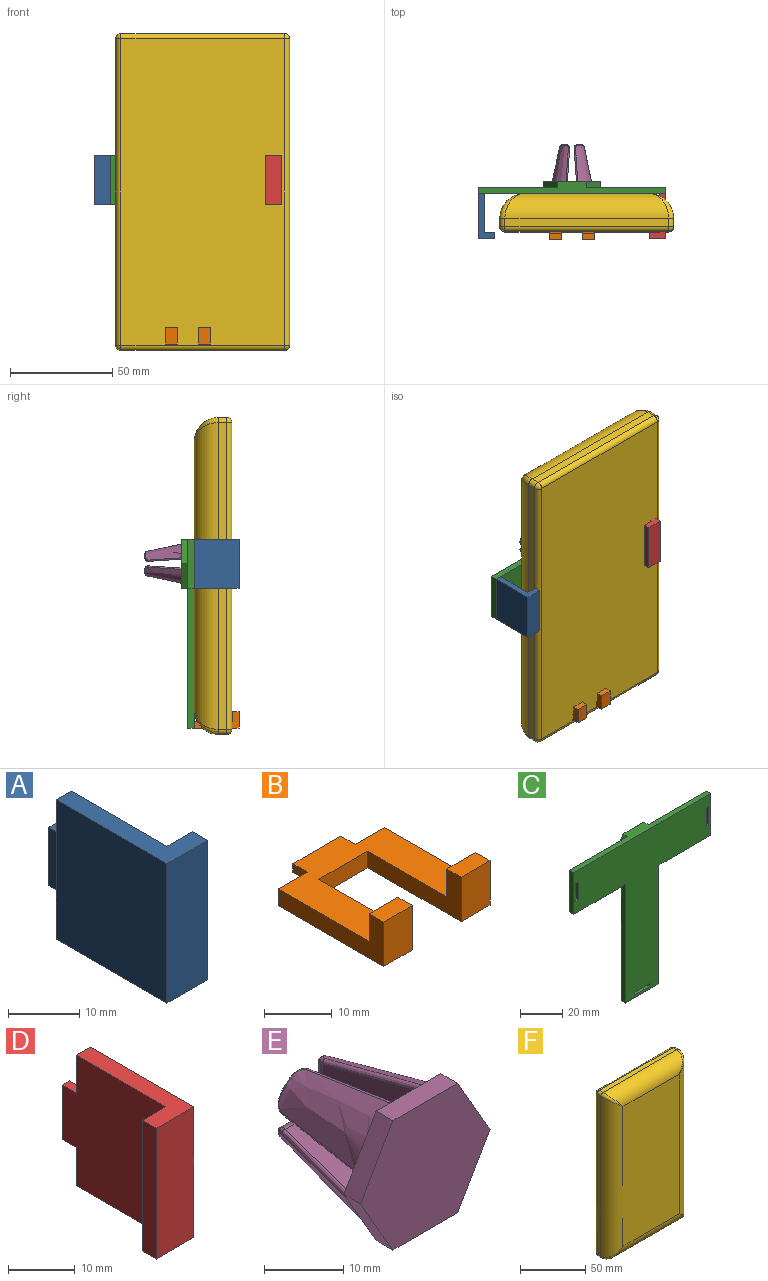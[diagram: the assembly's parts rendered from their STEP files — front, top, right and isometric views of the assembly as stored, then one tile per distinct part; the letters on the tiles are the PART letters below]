
ASSEMBLY  parts=6 mates=5
PART A: 12 faces, bbox 8x25x24 mm
  f0: plane 22x8mm, normal (0,0,-1), area 81mm2, adj f1,f4,f5,f6,f7,f11
  f1: plane 24x22mm, normal (1,0,0), area 486mm2, adj f0,f2,f3,f7,f8,f10,f11
  f2: plane 22x8mm, normal (0,0,1), area 81mm2, adj f1,f4,f5,f6,f7,f11
  f3: plane 10x1.5mm, normal (0,1,0), area 15mm2, adj f1,f8,f9,f10
  f4: plane 24x22mm, normal (-1,0,0), area 528mm2, adj f0,f2,f6,f11
  f5: plane 24x3mm, normal (1,0,0), area 72mm2, adj f0,f2,f6,f7
  f6: plane 24x8mm, normal (0,-1,0), area 192mm2, adj f0,f2,f4,f5
  f7: plane 24x5mm, normal (0,1,0), area 120mm2, adj f0,f1,f2,f5
  f8: plane 3x1.5mm, normal (0,0,1), area 4.5mm2, adj f1,f3,f9,f11
  f9: plane 10x3mm, normal (-1,0,0), area 30mm2, adj f3,f8,f10,f11
  f10: plane 3x1.5mm, normal (0,0,-1), area 4.5mm2, adj f1,f3,f9,f11
  f11: plane 24x3mm, normal (0,1,0), area 57mm2, adj f0,f1,f2,f4,f8,f9,f10
PART B: 18 faces, bbox 22.2x25x8 mm
  f0: plane 10x1.5mm, normal (0,1,0), area 15mm2, adj f1,f2,f3,f4
  f1: plane 22.2x22mm, normal (0,0,1), area 283.5mm2, adj f0,f3,f4,f5,f6,f7,f9,f12
  f2: plane 10x3mm, normal (0,0,-1), area 30mm2, adj f0,f3,f4,f5
  f3: plane 3x1.5mm, normal (-1,0,0), area 4.5mm2, adj f0,f1,f2,f5
  f4: plane 3x1.5mm, normal (1,0,0), area 4.5mm2, adj f0,f1,f2,f5
  f5: plane 22.2x3mm, normal (0,1,0), area 51.6mm2, adj f1,f2,f3,f4,f7,f8,f16
  f6: plane 19.5x8mm, normal (1,0,0), area 73.5mm2, adj f1,f8,f9,f10,f11,f17
  f7: plane 22x8mm, normal (-1,0,0), area 81mm2, adj f1,f5,f8,f9,f10,f11
  f8: plane 22.2x22mm, normal (0,0,-1), area 289.5mm2, adj f5,f6,f7,f11,f12,f15,f16,f17
  f9: plane 6x5mm, normal (0,1,0), area 30mm2, adj f1,f6,f7,f10
  f10: plane 6x3mm, normal (0,0,1), area 18mm2, adj f6,f7,f9,f11
  f11: plane 8x6mm, normal (0,-1,0), area 48mm2, adj f6,f7,f8,f10
  f12: plane 19.5x8mm, normal (-1,0,0), area 73.5mm2, adj f1,f8,f13,f14,f15,f17
  f13: plane 6x5mm, normal (0,1,0), area 30mm2, adj f1,f12,f14,f16
  f14: plane 6x3mm, normal (0,0,1), area 18mm2, adj f12,f13,f15,f16
  f15: plane 8x6mm, normal (0,-1,0), area 48mm2, adj f8,f12,f14,f16
  f16: plane 22x8mm, normal (1,0,0), area 81mm2, adj f1,f5,f8,f13,f14,f15
  f17: plane 10.2x3mm, normal (0,-1,0), area 30.6mm2, adj f1,f6,f8,f12
PART C: 35 faces, bbox 91.5x6x92.5 mm
  f0: plane 68.5x3mm, normal (-1,0,0), area 205.5mm2, adj f2,f3,f4,f5
  f1: plane 68.5x3mm, normal (1,0,0), area 205.5mm2, adj f2,f3,f4,f9
  f2: plane 22.2x3mm, normal (0,0,-1), area 66.6mm2, adj f0,f1,f3,f4
  f3: plane 92.5x91.5mm, normal (0,1,0), area 3169.4mm2, adj f0,f1,f2,f5,f6,f7,f8,f9
  f4: plane 92.5x91.5mm, normal (0,-1,0), area 3668.2mm2, adj f0,f1,f2,f5,f6,f7,f8,f9
  f5: plane 34.65x3mm, normal (0,0,-1), area 103.9mm2, adj f0,f3,f4,f8
  f6: plane 24x3mm, normal (1,0,0), area 72mm2, adj f3,f4,f7,f9
  f7: plane 91.5x6mm, normal (0,0,1), area 316.1mm2, adj f3,f4,f6,f8,f16,f17,f21
  f8: plane 24x3mm, normal (-1,0,0), area 72mm2, adj f3,f4,f5,f7
  f9: plane 34.65x3mm, normal (0,0,-1), area 103.9mm2, adj f1,f3,f4,f6
  f10: plane 10.1x5.83mm, normal (0.87,0,-0.5), area 35mm2, adj f11,f20,f21,f22
  f11: plane 10.1x5.83mm, normal (0.87,0,0.5), area 35mm2, adj f10,f12,f21,f22
  f12: plane 11.66x3mm, normal (0,0,1), area 35mm2, adj f11,f13,f21,f22
  f13: plane 10.1x5.83mm, normal (-0.87,0,0.5), area 35mm2, adj f12,f14,f21,f22
  f14: plane 10.1x5.83mm, normal (-0.87,0,-0.5), area 35mm2, adj f13,f20,f21,f22
  f15: plane 12x6.93mm, normal (-0.87,0,-0.5), area 41.6mm2, adj f3,f16,f19,f21
  f16: plane 12x6.93mm, normal (-0.87,0,0.5), area 41.6mm2, adj f3,f7,f15,f21
  f17: plane 12x6.93mm, normal (0.87,0,0.5), area 41.6mm2, adj f3,f7,f18,f21
  f18: plane 12x6.93mm, normal (0.87,0,-0.5), area 41.6mm2, adj f3,f17,f19,f21
  f19: plane 13.86x3mm, normal (0,0,-1), area 41.6mm2, adj f3,f15,f18,f21
  f20: plane 11.66x3mm, normal (0,0,-1), area 35mm2, adj f10,f14,f21,f22
  f21: plane 27.71x24mm, normal (0,1,0), area 145.5mm2, adj f7,f10,f11,f12,f13,f14,f15,f16
  f22: plane 23.33x20.2mm, normal (0,1,0), area 353.4mm2, adj f10,f11,f12,f13,f14,f20
  f23: plane 10.1x3mm, normal (1,0,0), area 30.3mm2, adj f3,f4,f24,f25
  f24: plane 3x1.6mm, normal (0,0,-1), area 4.8mm2, adj f3,f4,f23,f26
  f25: plane 3x1.6mm, normal (0,0,1), area 4.8mm2, adj f3,f4,f23,f26
  f26: plane 10.1x3mm, normal (-1,0,0), area 30.3mm2, adj f3,f4,f24,f25
  f27: plane 10.1x3mm, normal (0,0,1), area 30.3mm2, adj f3,f4,f28,f29
  f28: plane 3x1.6mm, normal (1,0,0), area 4.8mm2, adj f3,f4,f27,f30
  f29: plane 3x1.6mm, normal (-1,0,0), area 4.8mm2, adj f3,f4,f27,f30
  f30: plane 10.1x3mm, normal (0,0,-1), area 30.3mm2, adj f3,f4,f28,f29
  f31: plane 10.1x3mm, normal (1,0,0), area 30.3mm2, adj f3,f4,f32,f33
  f32: plane 3x1.6mm, normal (0,0,-1), area 4.8mm2, adj f3,f4,f31,f34
  f33: plane 3x1.6mm, normal (0,0,1), area 4.8mm2, adj f3,f4,f31,f34
  f34: plane 10.1x3mm, normal (-1,0,0), area 30.3mm2, adj f3,f4,f32,f33
PART D: 12 faces, bbox 8x25x24 mm
  f0: plane 22x8mm, normal (0,0,-1), area 81mm2, adj f1,f3,f5,f6,f7,f11
  f1: plane 24x22mm, normal (1,0,0), area 528mm2, adj f0,f4,f6,f11
  f2: plane 10x1.5mm, normal (0,1,0), area 15mm2, adj f3,f8,f9,f10
  f3: plane 24x22mm, normal (-1,0,0), area 486mm2, adj f0,f2,f4,f7,f8,f10,f11
  f4: plane 22x8mm, normal (0,0,1), area 81mm2, adj f1,f3,f5,f6,f7,f11
  f5: plane 24x3mm, normal (-1,0,0), area 72mm2, adj f0,f4,f6,f7
  f6: plane 24x8mm, normal (0,-1,0), area 192mm2, adj f0,f1,f4,f5
  f7: plane 24x5mm, normal (0,1,0), area 120mm2, adj f0,f3,f4,f5
  f8: plane 3x1.5mm, normal (0,0,-1), area 4.5mm2, adj f2,f3,f9,f11
  f9: plane 10x3mm, normal (1,0,0), area 30mm2, adj f2,f8,f10,f11
  f10: plane 3x1.5mm, normal (0,0,1), area 4.5mm2, adj f2,f3,f9,f11
  f11: plane 24x3mm, normal (0,1,0), area 57mm2, adj f0,f1,f3,f4,f8,f9,f10
PART E: 60 faces, bbox 23.2x23.4x20.6 mm
  f0: bspline ~17.61x8.12mm, area 143.4mm2, adj f4,f18,f19,f20,f48,f52
  f1: bspline ~17.61x8.12mm, area 143.4mm2, adj f4,f22,f23,f24,f43,f47
  f2: bspline ~17.61x8.12mm, area 143.4mm2, adj f4,f26,f27,f28,f38,f42
  f3: bspline ~17.61x8.12mm, area 143.4mm2, adj f4,f30,f31,f32,f33,f37
  f4: plane 23.15x20.06mm, normal (0,1,0), area 188.5mm2, adj f0,f1,f2,f3,f6,f7,f9,f10
  f5: plane 2.36x2.36mm, normal (0,1,0), area 3.3mm2, adj f31,f34,f36
  f6: plane 16.4x7.48mm, normal (-1,-0.07,0), area 85.4mm2, adj f4,f29,f32,f34
  f7: plane 16.4x7.48mm, normal (0,-0.07,-1), area 85.4mm2, adj f4,f29,f30,f36
  f8: plane 2.36x2.36mm, normal (0,1,0), area 3.3mm2, adj f27,f39,f41
  f9: plane 16.4x7.48mm, normal (1,-0.07,0), area 85.4mm2, adj f4,f25,f28,f39
  f10: plane 16.4x7.48mm, normal (0,-0.07,-1), area 85.4mm2, adj f4,f25,f26,f41
  f11: plane 2.36x2.36mm, normal (0,1,0), area 3.3mm2, adj f23,f44,f46
  f12: plane 16.4x7.48mm, normal (-1,-0.07,0), area 85.4mm2, adj f4,f21,f24,f44
  f13: plane 16.4x7.48mm, normal (0,-0.07,1), area 85.4mm2, adj f4,f21,f22,f46
  f14: plane 2.36x2.36mm, normal (0,1,0), area 3.3mm2, adj f19,f49,f51
  f15: plane 16.4x7.48mm, normal (0,-0.07,1), area 85.4mm2, adj f4,f17,f20,f49
  f16: plane 16.4x7.48mm, normal (1,-0.07,0), area 85.4mm2, adj f4,f17,f18,f51
  f17: cylinder r=0.5mm len=16.41mm, axis (-0.07,-1,-0.07), area 12.9mm2, adj f4,f15,f16,f50
  f18: bspline ~22.72x5.45mm, area 15.7mm2, adj f0,f4,f16,f52
  f19: bspline ~3.89x3.54mm, area 2.4mm2, adj f0,f14,f48,f52
  f20: bspline ~22.72x5.45mm, area 15.7mm2, adj f0,f4,f15,f48
  f21: cylinder r=0.5mm len=16.41mm, axis (0.07,-1,-0.07), area 12.9mm2, adj f4,f12,f13,f45
  f22: bspline ~22.72x5.45mm, area 15.7mm2, adj f1,f4,f13,f47
  f23: bspline ~3.89x3.54mm, area 2.4mm2, adj f1,f11,f43,f47
  f24: bspline ~22.72x5.45mm, area 15.7mm2, adj f1,f4,f12,f43
  f25: cylinder r=0.5mm len=16.41mm, axis (-0.07,-1,0.07), area 12.9mm2, adj f4,f9,f10,f40
  f26: bspline ~22.72x5.45mm, area 15.7mm2, adj f2,f4,f10,f42
  f27: bspline ~3.89x3.54mm, area 2.4mm2, adj f2,f8,f38,f42
  f28: bspline ~22.72x5.45mm, area 15.7mm2, adj f2,f4,f9,f38
  f29: cylinder r=0.5mm len=16.41mm, axis (-0.07,1,-0.07), area 12.9mm2, adj f4,f6,f7,f35
  f30: bspline ~20.18x4.91mm, area 15.7mm2, adj f3,f4,f7,f37
  f31: bspline ~3.62x3.43mm, area 2.4mm2, adj f3,f5,f33,f37
  f32: bspline ~20.18x4.91mm, area 15.7mm2, adj f3,f4,f6,f33
  f33: bspline ~2.03x1.75mm, area 1.9mm2, adj f3,f31,f32,f34
  f34: cylinder r=1.5mm len=4mm, axis (0,0,-1), area 7.8mm2, adj f5,f6,f33,f35
  f35: bspline ~1.76x1.5mm, area 0.9mm2, adj f29,f34,f36
  f36: cylinder r=1.5mm len=4mm, axis (-1,0,0), area 7.8mm2, adj f5,f7,f35,f37
  f37: bspline ~1.99x1.93mm, area 1.9mm2, adj f3,f30,f31,f36
  f38: bspline ~1.99x1.93mm, area 1.9mm2, adj f2,f27,f28,f39
  f39: cylinder r=1.5mm len=4mm, axis (0,0,-1), area 7.8mm2, adj f8,f9,f38,f40
  f40: bspline ~1.76x1.5mm, area 0.9mm2, adj f25,f39,f41
  f41: cylinder r=1.5mm len=4mm, axis (1,0,0), area 7.8mm2, adj f8,f10,f40,f42
  f42: bspline ~2.03x1.75mm, area 1.9mm2, adj f2,f26,f27,f41
  f43: bspline ~1.99x1.93mm, area 1.9mm2, adj f1,f23,f24,f44
  f44: cylinder r=1.5mm len=4mm, axis (0,0,1), area 7.8mm2, adj f11,f12,f43,f45
  f45: bspline ~1.76x1.5mm, area 0.9mm2, adj f21,f44,f46
  f46: cylinder r=1.5mm len=4mm, axis (-1,0,0), area 7.8mm2, adj f11,f13,f45,f47
  f47: bspline ~2.03x1.75mm, area 1.9mm2, adj f1,f22,f23,f46
  f48: bspline ~1.99x1.93mm, area 1.9mm2, adj f0,f19,f20,f49
  f49: cylinder r=1.5mm len=4mm, axis (1,0,0), area 7.8mm2, adj f14,f15,f48,f50
  f50: bspline ~1.76x1.5mm, area 0.9mm2, adj f17,f49,f51
  f51: cylinder r=1.5mm len=4mm, axis (0,0,1), area 7.8mm2, adj f14,f16,f50,f52
  f52: bspline ~2.03x1.75mm, area 1.9mm2, adj f0,f18,f19,f51
  f53: plane 11.55x3mm, normal (0,0,1), area 34.6mm2, adj f4,f54,f58,f59
  f54: plane 10x5.77mm, normal (0.87,0,0.5), area 34.6mm2, adj f4,f53,f55,f59
  f55: plane 10x5.77mm, normal (0.87,0,-0.5), area 34.6mm2, adj f4,f54,f56,f59
  f56: plane 11.55x3mm, normal (0,0,-1), area 34.6mm2, adj f4,f55,f57,f59
  f57: plane 10x5.77mm, normal (-0.87,0,-0.5), area 34.6mm2, adj f4,f56,f58,f59
  f58: plane 10x5.77mm, normal (-0.87,0,0.5), area 34.6mm2, adj f4,f53,f57,f59
  f59: plane 23.09x20mm, normal (0,-1,0), area 346.4mm2, adj f53,f54,f55,f56,f57,f58
PART F: 26 faces, bbox 85x18.5x155 mm
  f0: plane 80x4mm, normal (0,0,1), area 320mm2, adj f6,f9,f11,f20
  f1: plane 150x4mm, normal (-1,0,0), area 600mm2, adj f6,f7,f12,f19
  f2: plane 80x4mm, normal (0,0,-1), area 320mm2, adj f7,f8,f16,f23
  f3: plane 150x4mm, normal (1,0,0), area 600mm2, adj f8,f9,f15,f24
  f4: plane 131x61mm, normal (0,-1,0), area 7991mm2, adj f19,f20,f23,f24
  f5: plane 150x80mm, normal (0,1,0), area 12000mm2, adj f11,f12,f15,f16
  f6: cylinder r=2.5mm len=4mm, axis (0,-1,0), area 15.7mm2, adj f0,f1,f10,f18
  f7: cylinder r=2.5mm len=4mm, axis (0,1,0), area 15.7mm2, adj f1,f2,f14,f21
  f8: cylinder r=2.5mm len=4mm, axis (0,-1,0), area 15.7mm2, adj f2,f3,f17,f25
  f9: cylinder r=2.5mm len=4mm, axis (0,1,0), area 15.7mm2, adj f0,f3,f13,f22
  f10: sphere r=2.5mm, area 9.8mm2, adj f6,f11,f12
  f11: cylinder r=2.5mm len=80mm, axis (-1,0,0), area 314.2mm2, adj f0,f5,f10,f13
  f12: cylinder r=2.5mm len=150mm, axis (0,0,-1), area 589mm2, adj f1,f5,f10,f14
  f13: sphere r=2.5mm, area 9.8mm2, adj f9,f11,f15
  f14: sphere r=2.5mm, area 9.8mm2, adj f7,f12,f16
  f15: cylinder r=2.5mm len=150mm, axis (0,0,1), area 589mm2, adj f3,f5,f13,f17
  f16: cylinder r=2.5mm len=80mm, axis (1,0,0), area 314.2mm2, adj f2,f5,f14,f17
  f17: sphere r=2.5mm, area 9.8mm2, adj f8,f15,f16
  f18: bspline ~13.88x12mm, area 50.9mm2, adj f6,f19,f20
  f19: cylinder r=12mm len=150mm, axis (0,0,1), area 2697.3mm2, adj f1,f4,f18,f21
  f20: cylinder r=12mm len=80mm, axis (1,0,0), area 1377.8mm2, adj f0,f4,f18,f22
  f21: bspline ~13.88x12mm, area 50.9mm2, adj f7,f19,f23
  f22: bspline ~13.88x12mm, area 50.9mm2, adj f9,f20,f24
  f23: cylinder r=12mm len=80mm, axis (-1,0,0), area 1377.8mm2, adj f2,f4,f21,f25
  f24: cylinder r=12mm len=150mm, axis (0,0,-1), area 2697.3mm2, adj f3,f4,f22,f25
  f25: bspline ~13.88x12mm, area 50.9mm2, adj f8,f23,f24
PLACE A t=(-81.2,-40.39,27.55)mm
PLACE B t=(-94.2,-40.39,40.65)mm
PLACE C t=(-94.2,-40.39,27.55)mm
PLACE D t=(-107.2,-40.39,27.55)mm
PLACE E t=(-94.2,-57.39,27.55)mm
PLACE F rot(axis=(1,0,0),180deg) t=(-232.27,-78.89,-8.84)mm
MATE fastened B.f0 <-> C.f3  axis (0,1,0) through (-94.2,-57.39,-49.85)mm
MATE fastened E.f59 <-> C.f22  axis (0,-1,0) through (-94.2,-57.39,27.55)mm
MATE planar C.f4 <-> F.f4  axis (0,-1,0) through (-94.2,-60.39,8.73)mm
MATE fastened D.f2 <-> C.f3  axis (0,1,0) through (-49.95,-57.39,27.55)mm
MATE fastened A.f3 <-> C.f3  axis (0,1,0) through (-138.45,-57.39,27.55)mm
